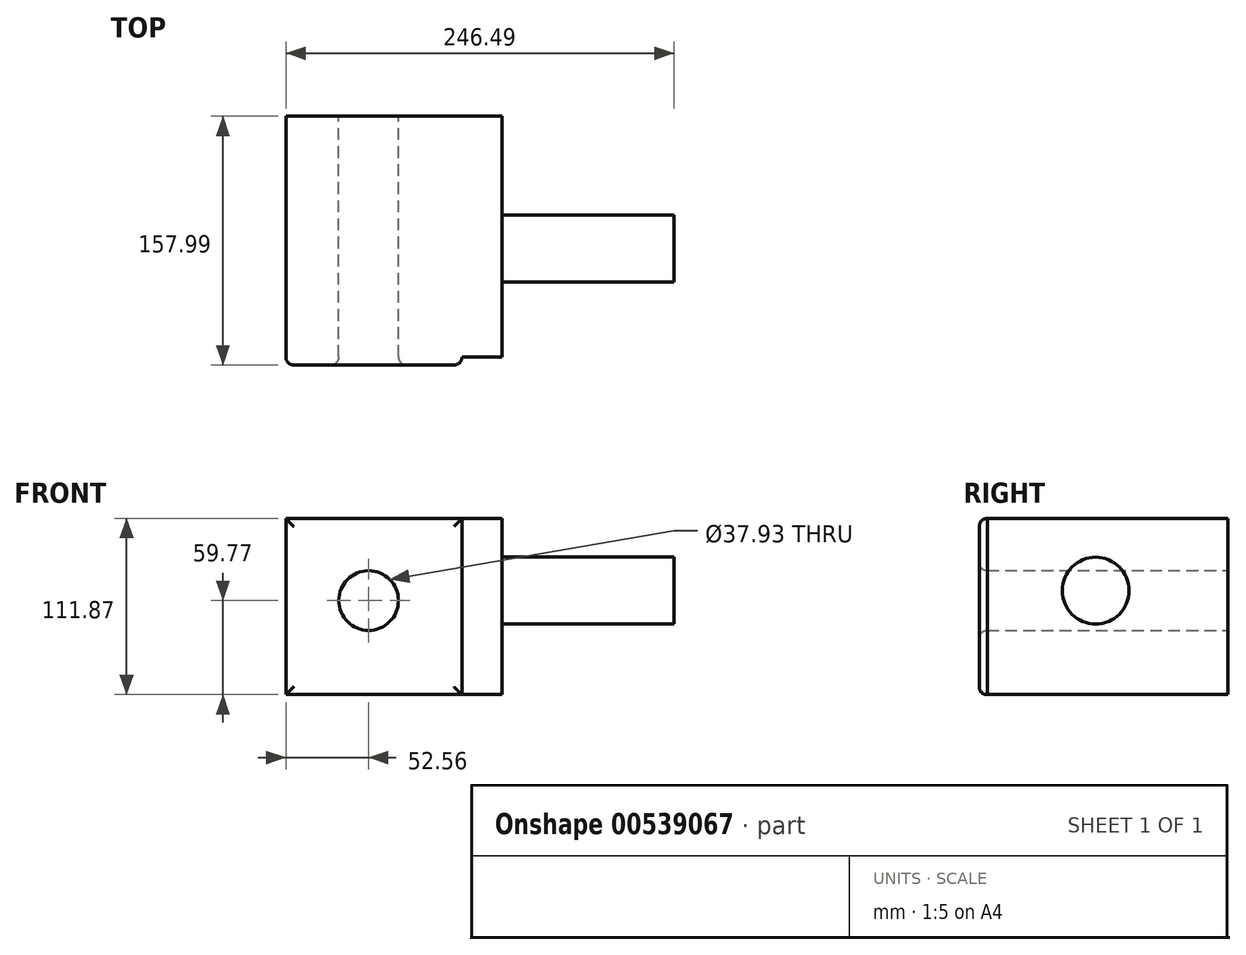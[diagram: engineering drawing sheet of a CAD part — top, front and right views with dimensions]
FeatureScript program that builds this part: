
annotation { "Feature Type Name" : "Feature", "Feature Type Description" : "" }
export const myFeature = defineFeature(function(context is Context, id is Id, definition is map)
    precondition{}
    {
        {
            var Q0;
            Q0=qCreatedBy(makeId("Front.planeOp"),FACE);
            var sketch = newSketch(context, id + "F0", { "sketchPlane" : qUnion([Q0])});
            skLineSegment(sketch, "E0.bottom", {"start": v(-52.56, 52.1) * mm, "end": v(59.3, 52.1) * mm});
            skLineSegment(sketch, "E0.top", {"start": v(-52.56, -59.77) * mm, "end": v(59.3, -59.77) * mm});
            skLineSegment(sketch, "E0.left", {"start": v(-52.56, 52.1) * mm, "end": v(-52.56, -59.77) * mm});
            skLineSegment(sketch, "E0.right", {"start": v(59.3, 52.1) * mm, "end": v(59.3, -59.77) * mm});
            skCircle(sketch, "E1", {"center": v(0, 0) * mm, "radius": 18.97 * mm});
            skSolve(sketch);
        }
        {
            var Q0;
            Q0=makeQuery(id+"F0.imprint","IMPRINT",FACE,{"disambiguationData":[TD([[makeQuery(id+"F0.imprint","IMPRINT",EDGE,{"derivedFrom":sQuery(id+"F0.wireOp",EDGE,"E0.bottom")}),-1.0]])]});
            extrude(context, id + "F1", {"entities" : qUnion([Q0]), "depth" : 158 * mm, "offsetDistance" : 25.4 * mm});
        }
        {
            var Q0;
            Q0=makeQuery(id+"F1.opExtrude","CAP_FACE",FACE,{"disambiguationData":[OSD([sQuery(id+"F0.wireOp",EDGE,"E0.bottom"),sQuery(id+"F0.wireOp",EDGE,"E0.top"),sQuery(id+"F0.wireOp",EDGE,"E0.left"),sQuery(id+"F0.wireOp",EDGE,"E0.right"),sQuery(id+"F0.wireOp",EDGE,"E1")])],"isStart":false});
            fillet(context, id + "F2", {"entities" : qUnion([Q0]), "radius" : 5.08 * mm, "tangentPropagation" : true, "allowEdgeOverflow" : false});
        }
        {
            var Q0;
            Q0=makeQuery(id+"F1.opExtrude","SWEPT_FACE",FACE,{"disambiguationData":[OSD([sQuery(id+"F0.wireOp",EDGE,"E0.right")])]});
            extrude(context, id + "F3", {"entities" : qUnion([Q0]), "operationType" : NewBodyOperationType.ADD, "depth" : 25.4 * mm, "offsetDistance" : 25.4 * mm});
        }
        {
            var Q0;
            Q0=makeQuery(id+"F3.opExtrude","CAP_FACE",FACE,{"disambiguationData":[OSD([sQuery(id+"F0.wireOp",EDGE,"E0.right")])],"isStart":false});
            var sketch = newSketch(context, id + "F4", { "sketchPlane" : qUnion([Q0])});
            skCircle(sketch, "E2", {"center": v(-84.04, 6.3) * mm, "radius": 21.24 * mm});
            skSolve(sketch);
        }
        {
            var Q0;
            Q0=makeQuery(id+"F4.imprint","IMPRINT",FACE,{"disambiguationData":[TD([[makeQuery(id+"F4.imprint","IMPRINT",EDGE,{"derivedFrom":sQuery(id+"F4.wireOp",EDGE,"E2")}),1.0]])]});
            extrude(context, id + "F5", {"entities" : qUnion([Q0]), "operationType" : NewBodyOperationType.ADD, "depth" : 109.22 * mm, "offsetDistance" : 25.4 * mm});
        }
    });
